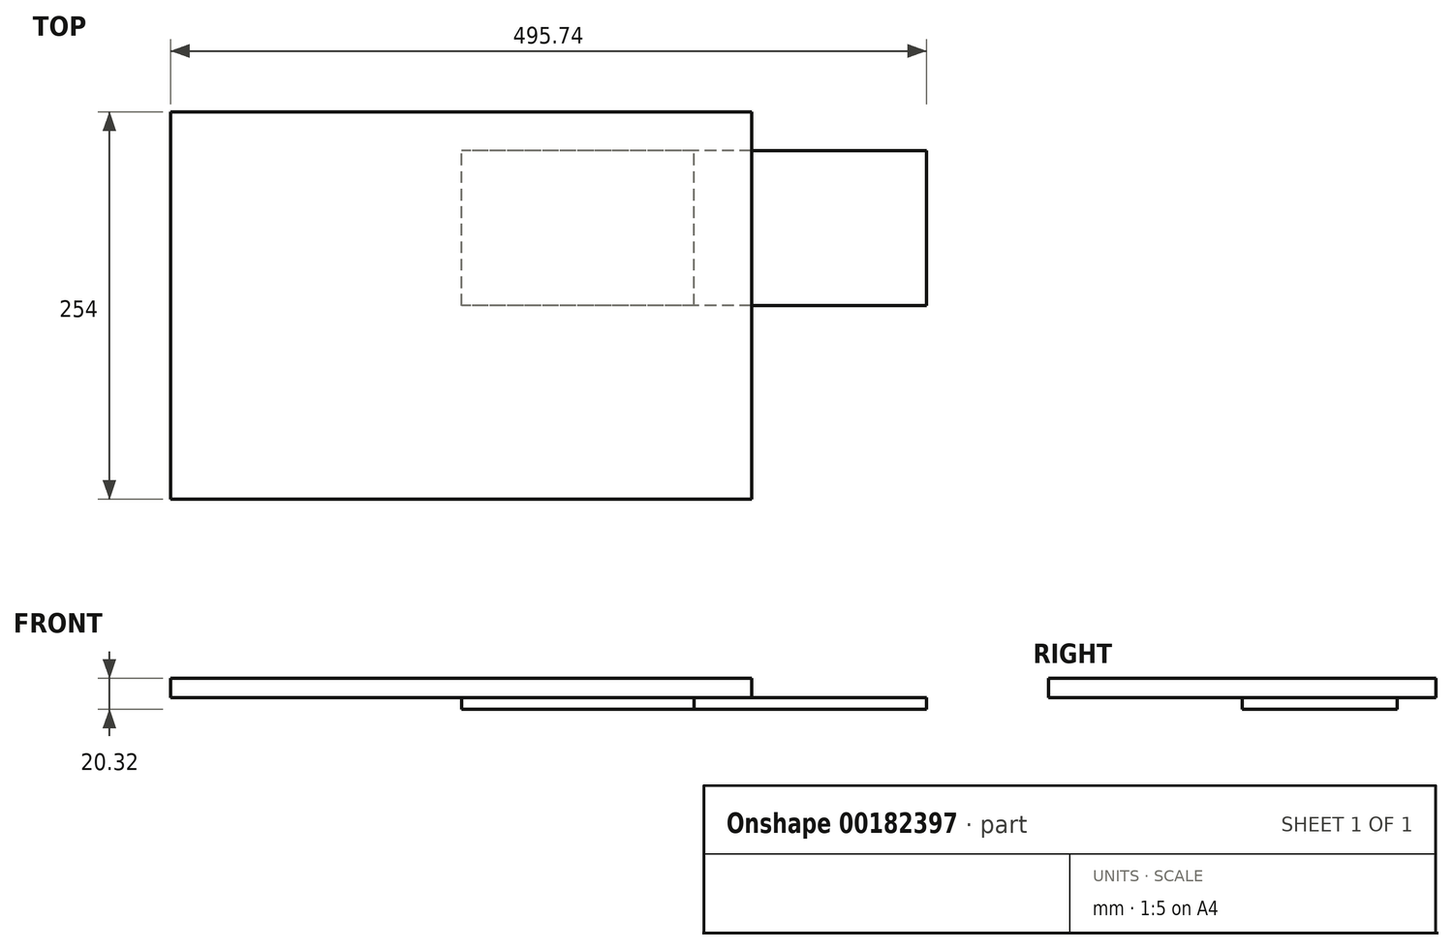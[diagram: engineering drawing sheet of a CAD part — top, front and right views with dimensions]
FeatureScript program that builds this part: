
annotation { "Feature Type Name" : "Feature", "Feature Type Description" : "" }
export const myFeature = defineFeature(function(context is Context, id is Id, definition is map)
    precondition{}
    {
        {
            var Q0;
            Q0=qCreatedBy(makeId("Front.planeOp"),FACE);
            var sketch = newSketch(context, id + "F0", { "sketchPlane" : qUnion([Q0])});
            skLineSegment(sketch, "E0.bottom", {"start": v(-190.94, 6.44) * mm, "end": v(190.06, 6.44) * mm});
            skLineSegment(sketch, "E0.top", {"start": v(-190.94, -6.26) * mm, "end": v(190.06, -6.26) * mm});
            skLineSegment(sketch, "E0.left", {"start": v(-190.94, 6.44) * mm, "end": v(-190.94, -6.26) * mm});
            skLineSegment(sketch, "E0.right", {"start": v(190.06, 6.44) * mm, "end": v(190.06, -6.26) * mm});
            skSolve(sketch);
        }
        {
            var Q0;
            Q0=makeQuery(id+"F0.imprint","IMPRINT",FACE,{"disambiguationData":[TD([[makeQuery(id+"F0.imprint","IMPRINT",EDGE,{"derivedFrom":sQuery(id+"F0.wireOp",EDGE,"E0.bottom")}),-1.0]])]});
            extrude(context, id + "F1", {"entities" : qUnion([Q0]), "depth" : 254 * mm});
        }
        {
            var Q0;
            Q0=qCreatedBy(makeId("Right.planeOp"),FACE);
            var sketch = newSketch(context, id + "F2", { "sketchPlane" : qUnion([Q0])});
            skLineSegment(sketch, "E1.bottom", {"start": v(-127, -6.26) * mm, "end": v(-25.4, -6.26) * mm});
            skLineSegment(sketch, "E1.top", {"start": v(-127, -13.88) * mm, "end": v(-25.4, -13.88) * mm});
            skLineSegment(sketch, "E1.left", {"start": v(-127, -6.26) * mm, "end": v(-127, -13.88) * mm});
            skLineSegment(sketch, "E1.right", {"start": v(-25.4, -6.26) * mm, "end": v(-25.4, -13.88) * mm});
            skSolve(sketch);
        }
        {
            var Q0;
            Q0=makeQuery(id+"F2.imprint","IMPRINT",FACE,{"disambiguationData":[TD([[makeQuery(id+"F2.imprint","IMPRINT",EDGE,{"derivedFrom":sQuery(id+"F2.wireOp",EDGE,"E1.bottom")}),-1.0]])]});
            extrude(context, id + "F3", {"entities" : qUnion([Q0]), "depth" : 152.4 * mm});
        }
        {
            var Q0;
            Q0=makeQuery(id+"F2.imprint","IMPRINT",FACE,{"disambiguationData":[TD([[makeQuery(id+"F2.imprint","IMPRINT",EDGE,{"derivedFrom":sQuery(id+"F2.wireOp",EDGE,"E1.bottom")}),-1.0]])]});
            extrude(context, id + "F4", {"entities" : qUnion([Q0]), "depth" : 304.8 * mm});
        }
    });
